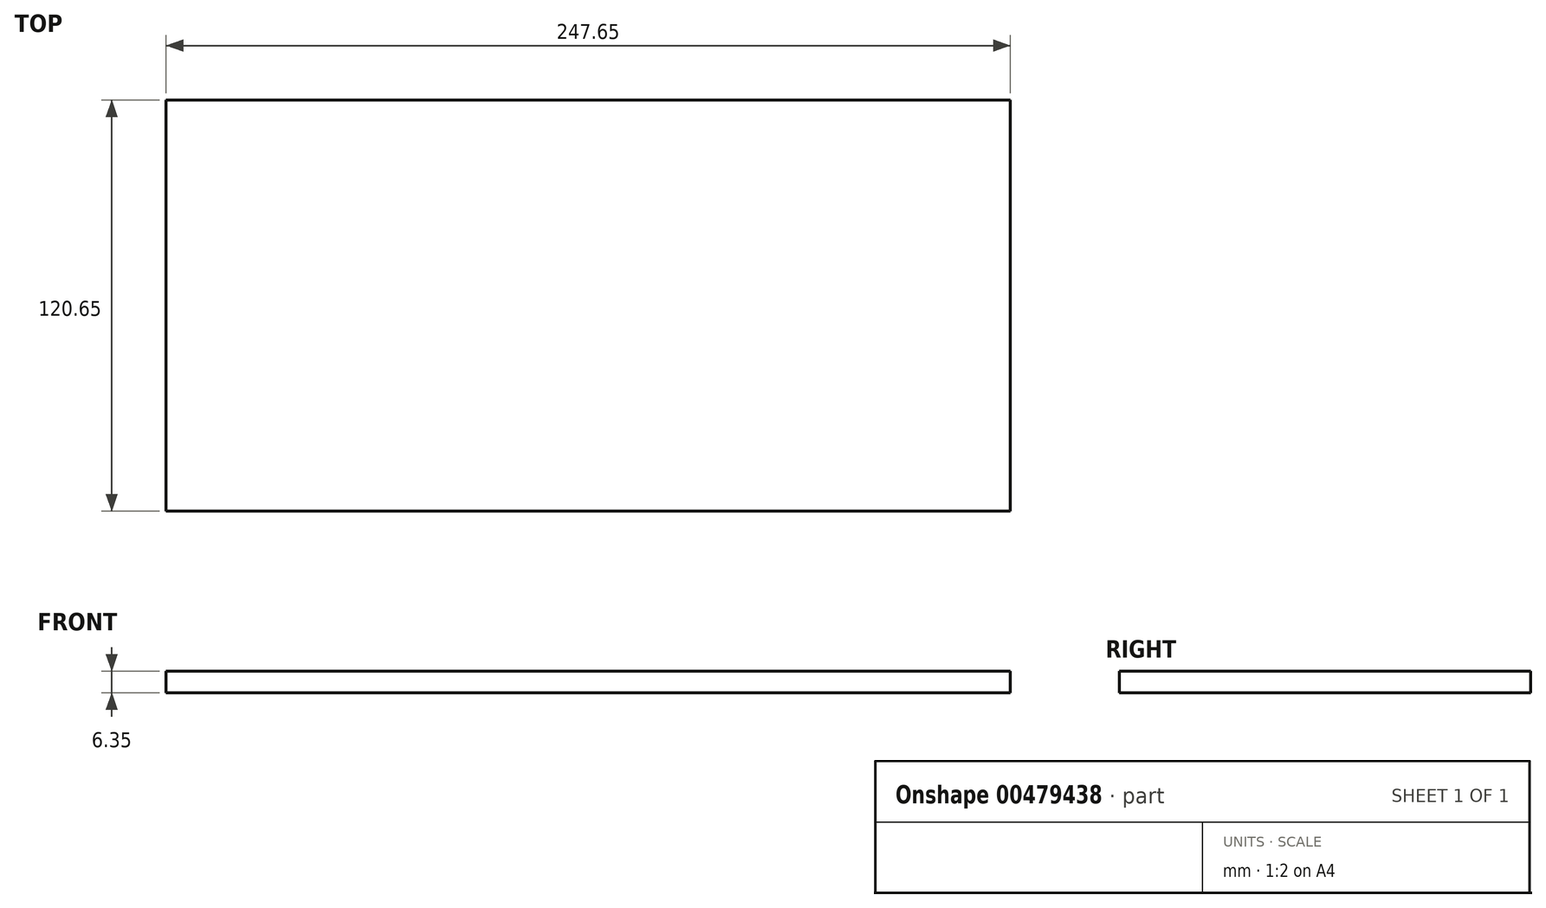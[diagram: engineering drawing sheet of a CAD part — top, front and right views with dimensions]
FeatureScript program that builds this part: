
annotation { "Feature Type Name" : "Feature", "Feature Type Description" : "" }
export const myFeature = defineFeature(function(context is Context, id is Id, definition is map)
    precondition{}
    {
        {
            var Q0;
            Q0=qCreatedBy(makeId("Top.planeOp"),FACE);
            var sketch = newSketch(context, id + "F0", { "sketchPlane" : qUnion([Q0])});
            skLineSegment(sketch, "E0.bottom", {"start": v(0, 0) * mm, "end": v(247.65, 0) * mm});
            skLineSegment(sketch, "E0.top", {"start": v(0, 120.65) * mm, "end": v(247.65, 120.65) * mm});
            skLineSegment(sketch, "E0.left", {"start": v(0, 0) * mm, "end": v(0, 120.65) * mm});
            skLineSegment(sketch, "E0.right", {"start": v(247.65, 0) * mm, "end": v(247.65, 120.65) * mm});
            skSolve(sketch);
        }
        {
            var Q0;
            Q0 = qSketchRegion(id + "F0", true);
            extrude(context, id + "F1", {"entities" : qUnion([Q0]), "depth" : 6.35 * mm});
        }
    });
